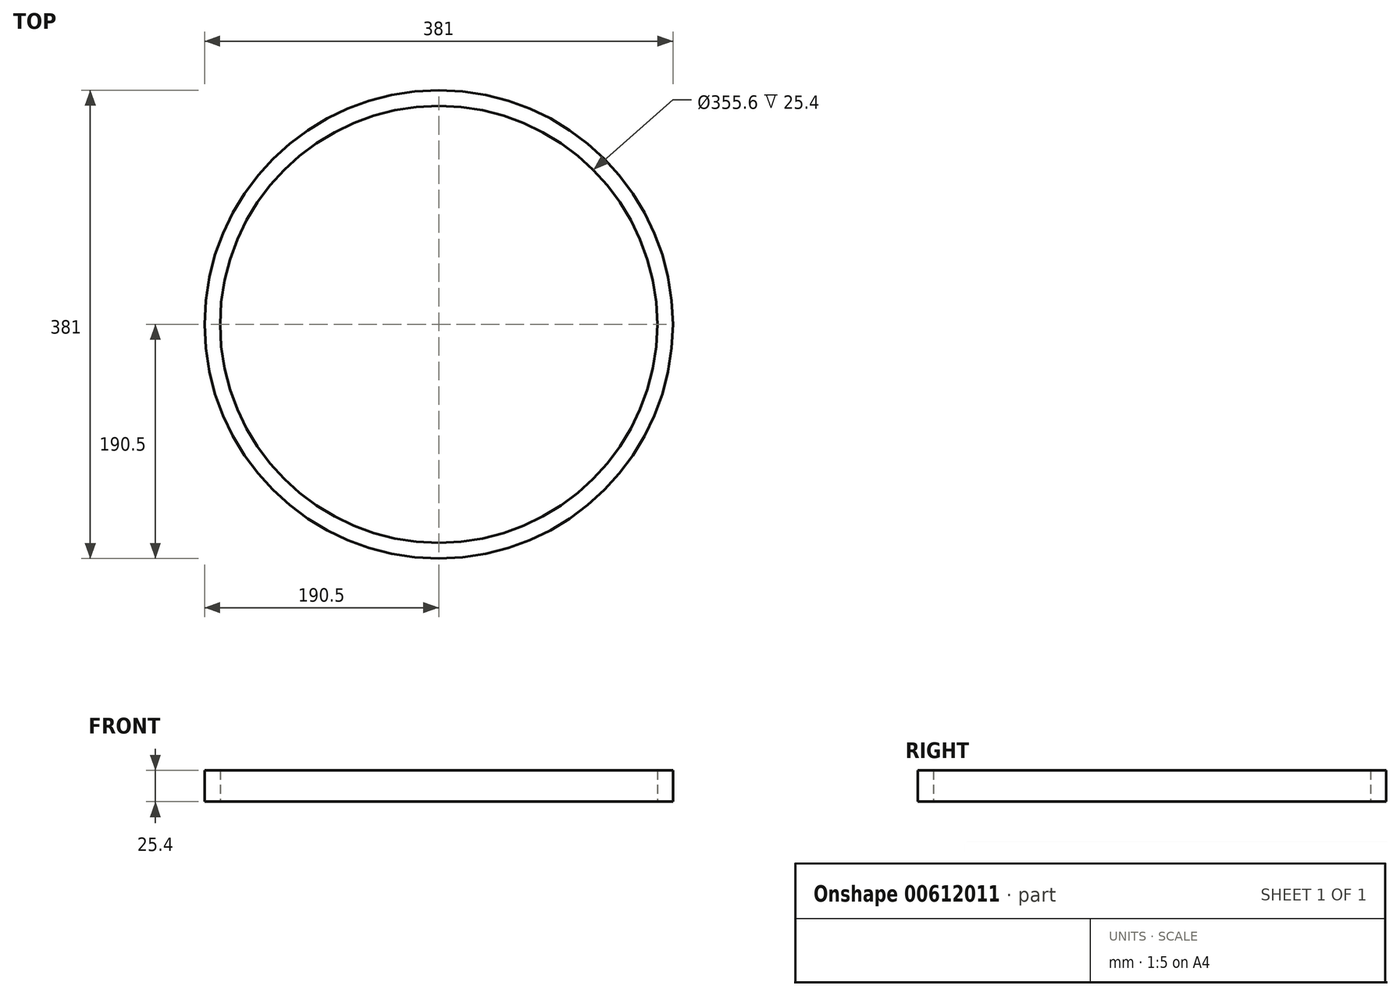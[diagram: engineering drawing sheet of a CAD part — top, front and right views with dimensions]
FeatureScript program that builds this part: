
annotation { "Feature Type Name" : "Feature", "Feature Type Description" : "" }
export const myFeature = defineFeature(function(context is Context, id is Id, definition is map)
    precondition{}
    {
        {
            var Q0;
            Q0=qCreatedBy(makeId("Top.planeOp"),FACE);
            var sketch = newSketch(context, id + "F0", { "sketchPlane" : qUnion([Q0])});
            skCircle(sketch, "E0", {"center": v(0, 0) * mm, "radius": 139.7 * mm});
            skCircle(sketch, "E1", {"center": v(0, 0) * mm, "radius": 190.5 * mm});
            skCircle(sketch, "E2", {"center": v(0, 0) * mm, "radius": 177.8 * mm});
            skCircle(sketch, "E3", {"center": v(0, 0) * mm, "radius": 171.45 * mm});
            skCircle(sketch, "E4", {"center": v(0, 0) * mm, "radius": 151.38 * mm});
            skSolve(sketch);
        }
        {
            var Q0;
            Q0 = qSketchRegion(id + "F0", true);
            extrude(context, id + "F1", {"entities" : qUnion([Q0]), "depth" : 25.4 * mm, "offsetDistance" : 25 * mm});
        }
    });
